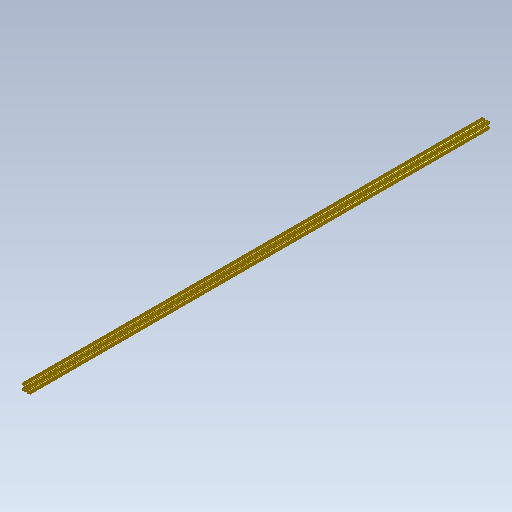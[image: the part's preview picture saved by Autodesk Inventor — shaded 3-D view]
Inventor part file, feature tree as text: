
AUTODESK INVENTOR PART (.ipt)
format: ipt  version: 2025.2 (Build 292293000, 293)  size: 445,952 bytes
history: native  units: mm
features: mirror x3, sketch x3, other x1, extrude x1
ambient origin geometry x8: Origin, YZ Plane, XZ Plane, XY Plane, X Axis, Y Axis, Z Axis, Center Point
bodies: Body1 (feature_tree)
feature tree (8):
  other  "Sólido1"
  extrude  "Extrusão1"  Depth=30.0mm
  mirror  "Espelhar1"
  mirror  "Espelhar2"
  mirror  "Espelhar3"
  sketch  "Esboço1"  dims[d0=10.0mm d2=30.0mm]
  sketch  "Esboço - Padrão circular1"  dims[d3=15.0mm]
  sketch  "Esboço - Padrão circular2"  dims[d8=80.0mm d10=360.0deg d14=9.0mm d15=2.2mm d17=2.0mm d19=2.2mm d22=40.0mm d24=360.0deg d26=8.2mm d32=4.5mm d33=1.1mm d34=11.5mm d37=2000.0mm d38=0.0mm]
